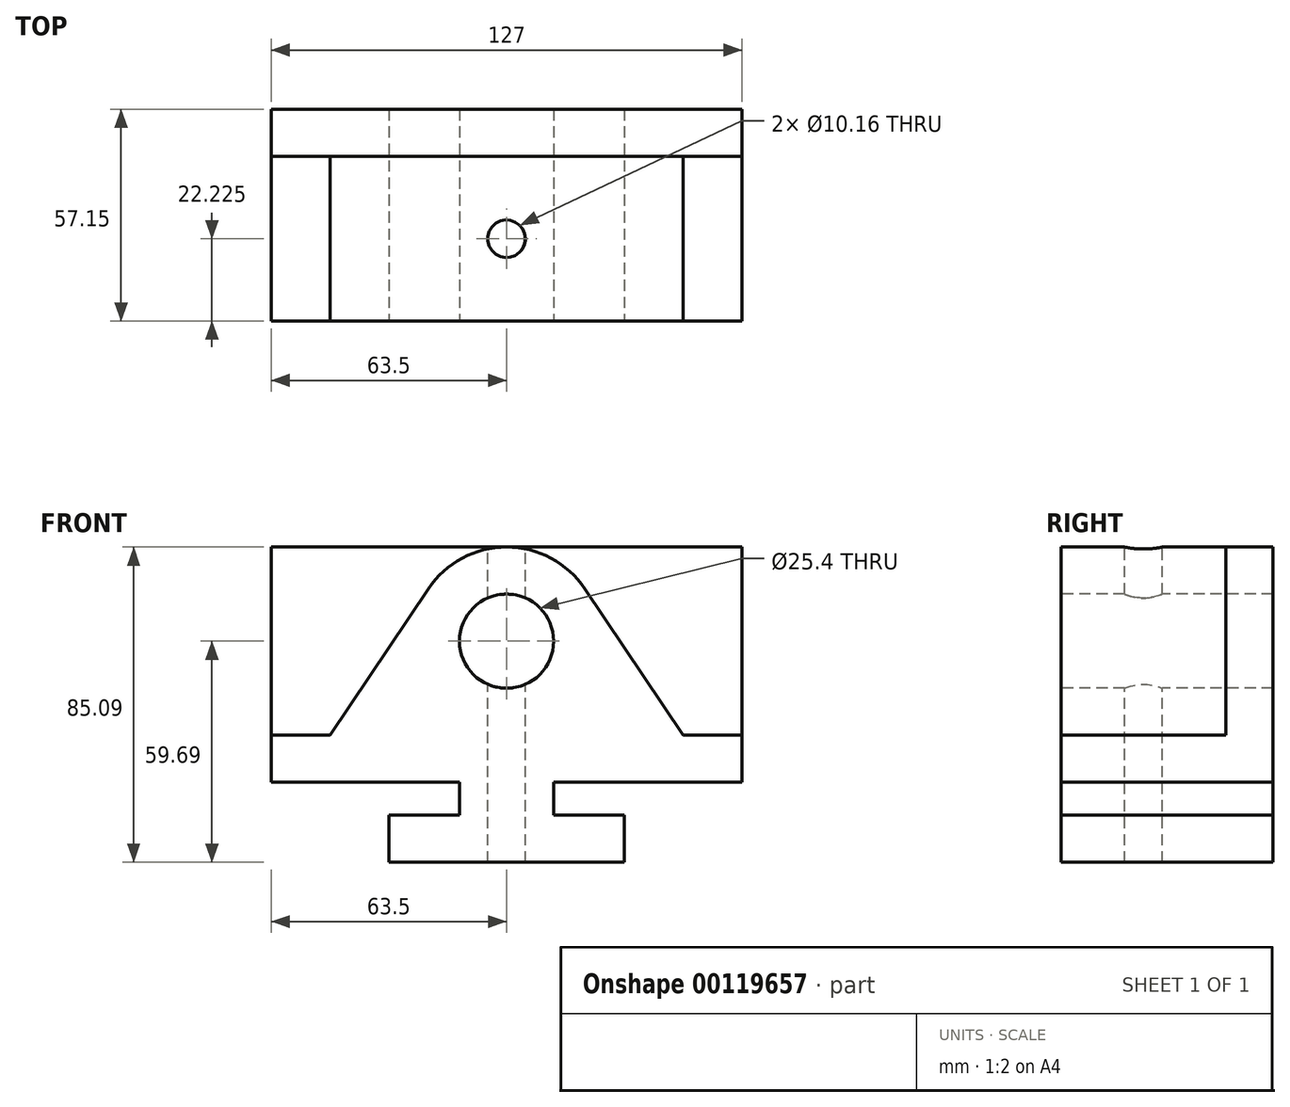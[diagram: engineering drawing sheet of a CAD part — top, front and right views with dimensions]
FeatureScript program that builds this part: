
annotation { "Feature Type Name" : "Feature", "Feature Type Description" : "" }
export const myFeature = defineFeature(function(context is Context, id is Id, definition is map)
    precondition{}
    {
        {
            var Q0;
            Q0=qCreatedBy(makeId("Front.planeOp"),FACE);
            var sketch = newSketch(context, id + "F0", { "sketchPlane" : qUnion([Q0])});
            skLineSegment(sketch, "E0", {"start": v(63.5, 0) * mm, "end": v(63.5, 63.5) * mm});
            skLineSegment(sketch, "E1", {"start": v(63.5, 63.5) * mm, "end": v(-63.5, 63.5) * mm});
            skLineSegment(sketch, "E2", {"start": v(-63.5, 63.5) * mm, "end": v(-63.5, 0) * mm});
            skLineSegment(sketch, "E3", {"start": v(-63.5, 0) * mm, "end": v(-12.7, 0) * mm});
            skLineSegment(sketch, "E4", {"start": v(-12.7, 0) * mm, "end": v(-12.7, -8.89) * mm});
            skLineSegment(sketch, "E5", {"start": v(-12.7, -8.89) * mm, "end": v(-31.75, -8.89) * mm});
            skLineSegment(sketch, "E6", {"start": v(-31.75, -8.9) * mm, "end": v(-31.75, -21.6) * mm});
            skLineSegment(sketch, "E7", {"start": v(-31.75, -21.59) * mm, "end": v(31.75, -21.59) * mm});
            skLineSegment(sketch, "E8", {"start": v(31.75, -21.6) * mm, "end": v(31.75, -8.9) * mm});
            skLineSegment(sketch, "E9", {"start": v(31.75, -8.89) * mm, "end": v(12.7, -8.89) * mm});
            skLineSegment(sketch, "E10", {"start": v(12.7, -8.89) * mm, "end": v(12.7, 0) * mm});
            skLineSegment(sketch, "E11", {"start": v(12.7, 0) * mm, "end": v(63.5, 0) * mm});
            skLineSegment(sketch, "E12", {"start": v(-12.7, 0) * mm, "end": v(12.7, 0) * mm, "construction": true});
            skPoint(sketch, "E13", {"position": v(0, 0) * mm});
            skSolve(sketch);
        }
        {
            var Q0;
            Q0=makeQuery(id+"F0.imprint","IMPRINT",FACE,{"disambiguationData":[TD([[makeQuery(id+"F0.imprint","IMPRINT",EDGE,{"derivedFrom":sQuery(id+"F0.wireOp",EDGE,"E0")}),1.0]])]});
            extrude(context, id + "F1", {"entities" : qUnion([Q0]), "oppositeDirection" : true, "depth" : 57.15 * mm});
        }
        {
            var Q0;
            Q0=makeQuery(id+"F0.imprint","IMPRINT",FACE,{"disambiguationData":[TD([[makeQuery(id+"F0.imprint","IMPRINT",EDGE,{"derivedFrom":sQuery(id+"F0.wireOp",EDGE,"E0")}),1.0]])]});
            var sketch = newSketch(context, id + "F2", { "sketchPlane" : qUnion([Q0])});
            skLineSegment(sketch, "E14", {"start": v(-21.1, 52.25) * mm, "end": v(-47.62, 12.7) * mm});
            skLineSegment(sketch, "E15", {"start": v(-47.63, 12.7) * mm, "end": v(-63.5, 12.7) * mm});
            skLineSegment(sketch, "E16", {"start": v(-63.5, 12.7) * mm, "end": v(-63.5, 0) * mm, "construction": true});
            skLineSegment(sketch, "E17", {"start": v(21.1, 52.25) * mm, "end": v(47.62, 12.7) * mm});
            skLineSegment(sketch, "E18", {"start": v(47.63, 12.7) * mm, "end": v(63.5, 12.7) * mm});
            skLineSegment(sketch, "E19", {"start": v(63.5, 12.7) * mm, "end": v(63.5, 0) * mm, "construction": true});
            skArc(sketch, "E20", {"start": v(21.1, 52.25) * mm, "mid": v(0, 63.5) * mm, "end": v(-21.1, 52.25) * mm});
            skPoint(sketch, "E21", {"position": v(0, 63.5) * mm});
            skLineSegment(sketch, "E22", {"start": v(-63.5, 12.7) * mm, "end": v(-63.5, 63.5) * mm});
            skLineSegment(sketch, "E23", {"start": v(-63.5, 63.5) * mm, "end": v(0, 63.5) * mm});
            skLineSegment(sketch, "E24", {"start": v(0, 63.5) * mm, "end": v(63.5, 63.5) * mm});
            skLineSegment(sketch, "E25", {"start": v(63.5, 63.5) * mm, "end": v(63.5, 12.7) * mm});
            skCircle(sketch, "E26", {"center": v(0, 38.1) * mm, "radius": 12.7 * mm});
            skSolve(sketch);
        }
        {
            var Q0;
            {var subQ1=sQuery(id+"F2.wireOp",EDGE,"E17");Q0=makeQuery(id+"F2.imprint","IMPRINT",FACE,{"disambiguationData":[TD([[makeQuery(id+"F2.imprint","IMPRINT",EDGE,{"derivedFrom":subQ1}),1.0]])]});}
            extrude(context, id + "F3", {"entities" : qUnion([Q0]), "operationType" : NewBodyOperationType.REMOVE, "oppositeDirection" : true, "depth" : 44.45 * mm});
        }
        {
            var Q0;
            {var subQ1=sQuery(id+"F2.wireOp",EDGE,"E14");Q0=makeQuery(id+"F2.imprint","IMPRINT",FACE,{"disambiguationData":[TD([[makeQuery(id+"F2.imprint","IMPRINT",EDGE,{"derivedFrom":subQ1}),-1.0]])]});}
            extrude(context, id + "F4", {"entities" : qUnion([Q0]), "operationType" : NewBodyOperationType.REMOVE, "oppositeDirection" : true, "depth" : 44.45 * mm});
        }
        {
            var Q0;
            Q0=makeQuery(id+"F2.imprint","IMPRINT",FACE,{"disambiguationData":[TD([[makeQuery(id+"F2.imprint","IMPRINT",EDGE,{"derivedFrom":sQuery(id+"F2.wireOp",EDGE,"E26")}),1.0]])]});
            extrude(context, id + "F5", {"entities" : qUnion([Q0]), "operationType" : NewBodyOperationType.REMOVE, "endBound" : BoundingType.THROUGH_ALL, "oppositeDirection" : true, "depth" : 25.4 * mm});
        }
        {
            var Q0;
            Q0=makeQuery(id+"F1.opExtrude","SWEPT_FACE",FACE,{"disambiguationData":[OSD([sQuery(id+"F0.wireOp",EDGE,"E1")])]});
            var sketch = newSketch(context, id + "F6", { "sketchPlane" : qUnion([Q0])});
            skCircle(sketch, "E27", {"center": v(0, 22.23) * mm, "radius": 5.08 * mm});
            skSolve(sketch);
        }
        {
            var Q0;
            Q0=makeQuery(id+"F6.imprint","IMPRINT",FACE,{"disambiguationData":[TD([[makeQuery(id+"F6.imprint","IMPRINT",EDGE,{"derivedFrom":sQuery(id+"F6.wireOp",EDGE,"E27")}),1.0]])]});
            var Q1;
            Q1=sQuery(id+"F6.wireOp",EDGE,"E27");
            extrude(context, id + "F7", {"entities" : qUnion([Q0]), "operationType" : NewBodyOperationType.REMOVE, "surfaceEntities" : qUnion([Q1]), "endBound" : BoundingType.THROUGH_ALL, "oppositeDirection" : true, "depth" : 25.4 * mm});
        }
    });
